# Revit family: ШУЗ_ШУЗ-С300_17.03.25
name_source: partatom
category: Оборудование
units: mm (PartAtom-declared; Revit-internal decimal feet)

## family parameters
Всегда вертикально = Да
Классификация = Нет
На основе рабочей плоскости = Нет
Общий = Нет
При загрузке вырезать с полостями = Нет
Размер круглого соединителя = Использовать диаметр
Тип детали = Нормальный
Точка расчета площади = Нет

## types (1)
- ШУЗ_ШУЗ-С300
    URL = https://plazma-t.ru
    Изготовитель = ООО "Плазма-Т"
    Комментарии к типоразмеру = Ш1/DEK
    Назв ПУШ = 179 мм
    Описание = ШУЗ-М предназначен для управления одно/трехфазным электроприводом задвижки практически любого производителя из известных на рынке. Управление осуществляется в режиме «Местный пуск» с лицевой панели ШУЗ-М или по сигналам любого модуля или прибора управления пожарного в режиме «Автоматический пуск» с отображением состояния задвижки при помощи световой индикации и с передачей сигналов состояния на модуль управления.
    Отметка по умолчанию = 0 мм
    Расст ПУШ = 80 мм
    Расст ввод = 60 мм
    Расст ввод 2 = 55 мм
    Расст замок = 55 мм
    выход 3 = Да
    расст вывод = 55 мм
